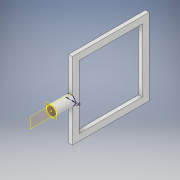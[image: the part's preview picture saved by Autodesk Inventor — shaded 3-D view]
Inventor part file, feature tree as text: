
AUTODESK INVENTOR PART (.ipt)
format: ipt  version: 2019 (Build 230136000, 136)  size: 125,952 bytes
history: native  units: mm
features: sketch x7, other x4, extrude x2
ambient origin geometry x8: Origin, YZ Plane, XZ Plane, XY Plane, X Axis, Y Axis, Z Axis, Center Point
bodies: Solide1 (feature_tree)
feature tree (13):
  other  "Coupe1"
  sketch  "Esquisse 3D1"
  sketch  "Esquisse 3D2"
  extrude  "Extrusion1"  Depth=50.0mm
  sketch  "Esquisse2"
  sketch  "Esquisse3"
  other  "Plan de construction1"
  extrude  "Extrusion2"  Depth=200.0mm TaperAngle=0.0deg
  other  "Plan de construction2"
  sketch  "Esquisse5"
  sketch  "Esquisse1"
  sketch  "Esquisse4"
  other  "Projeter les arêtes coupées1"
